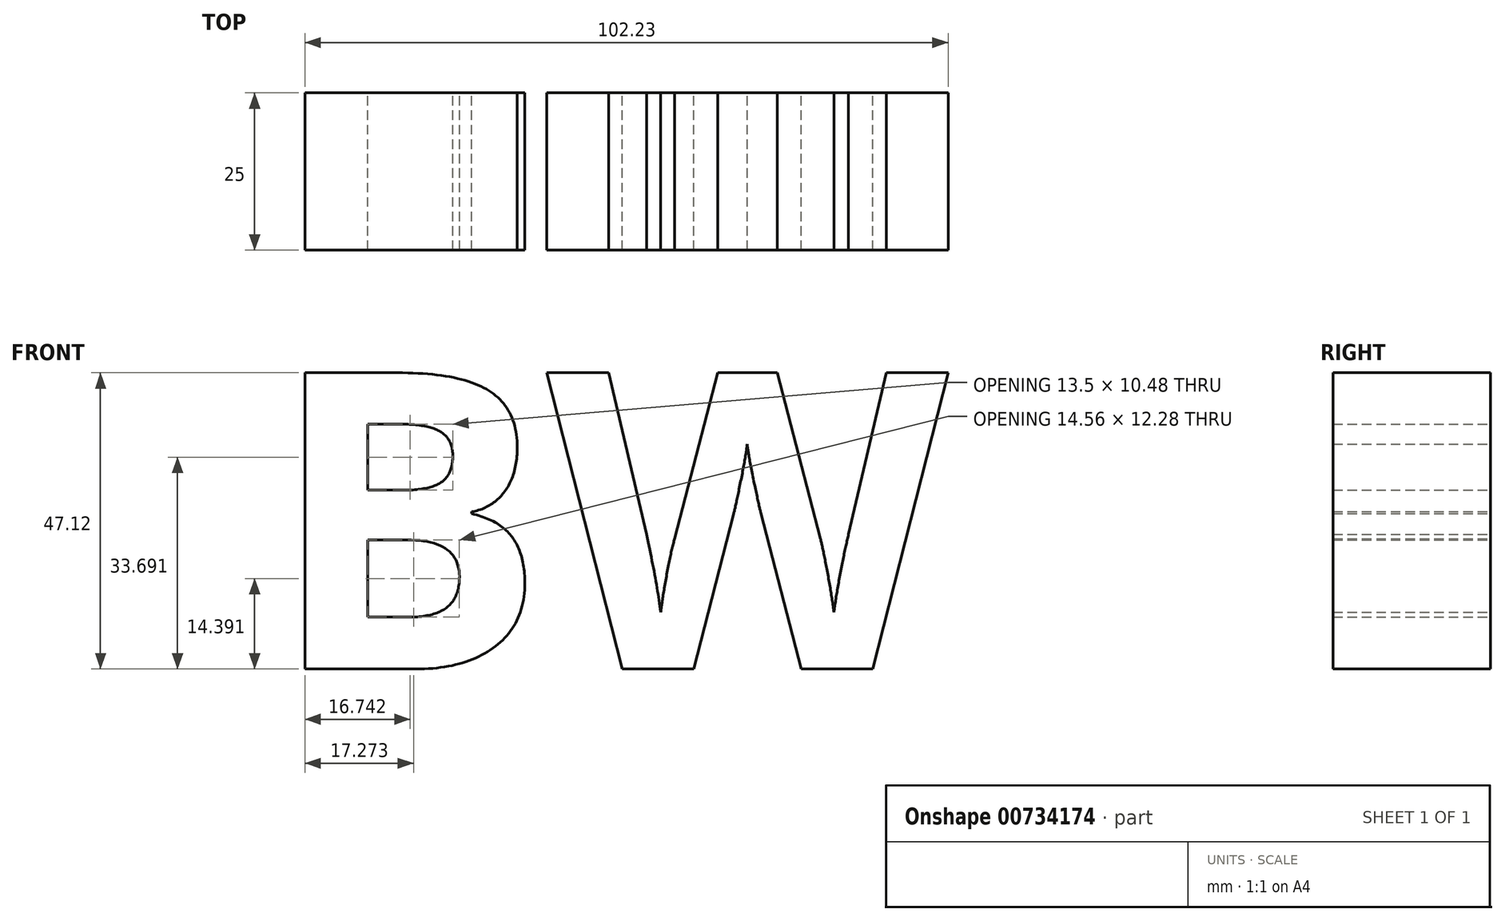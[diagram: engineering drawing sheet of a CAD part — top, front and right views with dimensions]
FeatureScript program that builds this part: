
annotation { "Feature Type Name" : "Feature", "Feature Type Description" : "" }
export const myFeature = defineFeature(function(context is Context, id is Id, definition is map)
    precondition{}
    {
        {
            var Q0;
            Q0=qCreatedBy(makeId("Front.planeOp"),FACE);
            var sketch = newSketch(context, id + "F0", { "sketchPlane" : qUnion([Q0])});
            skText(sketch, "E0", { "text": "BW\n", "fontName": "OpenSans-Bold.ttf"});
            const initialGuessF0  = {"E0": [-0.01285, -0.0032, 1, 0, 0.04752]};
            skSetInitialGuess(sketch, initialGuessF0);
            skSolve(sketch);
        }
        {
            var Q0;
            Q0 = qSketchRegion(id + "F0", true);
            extrude(context, id + "F1", {"entities" : qUnion([Q0]), "depth" : 25 * mm, "offsetDistance" : 25 * mm});
        }
    });
